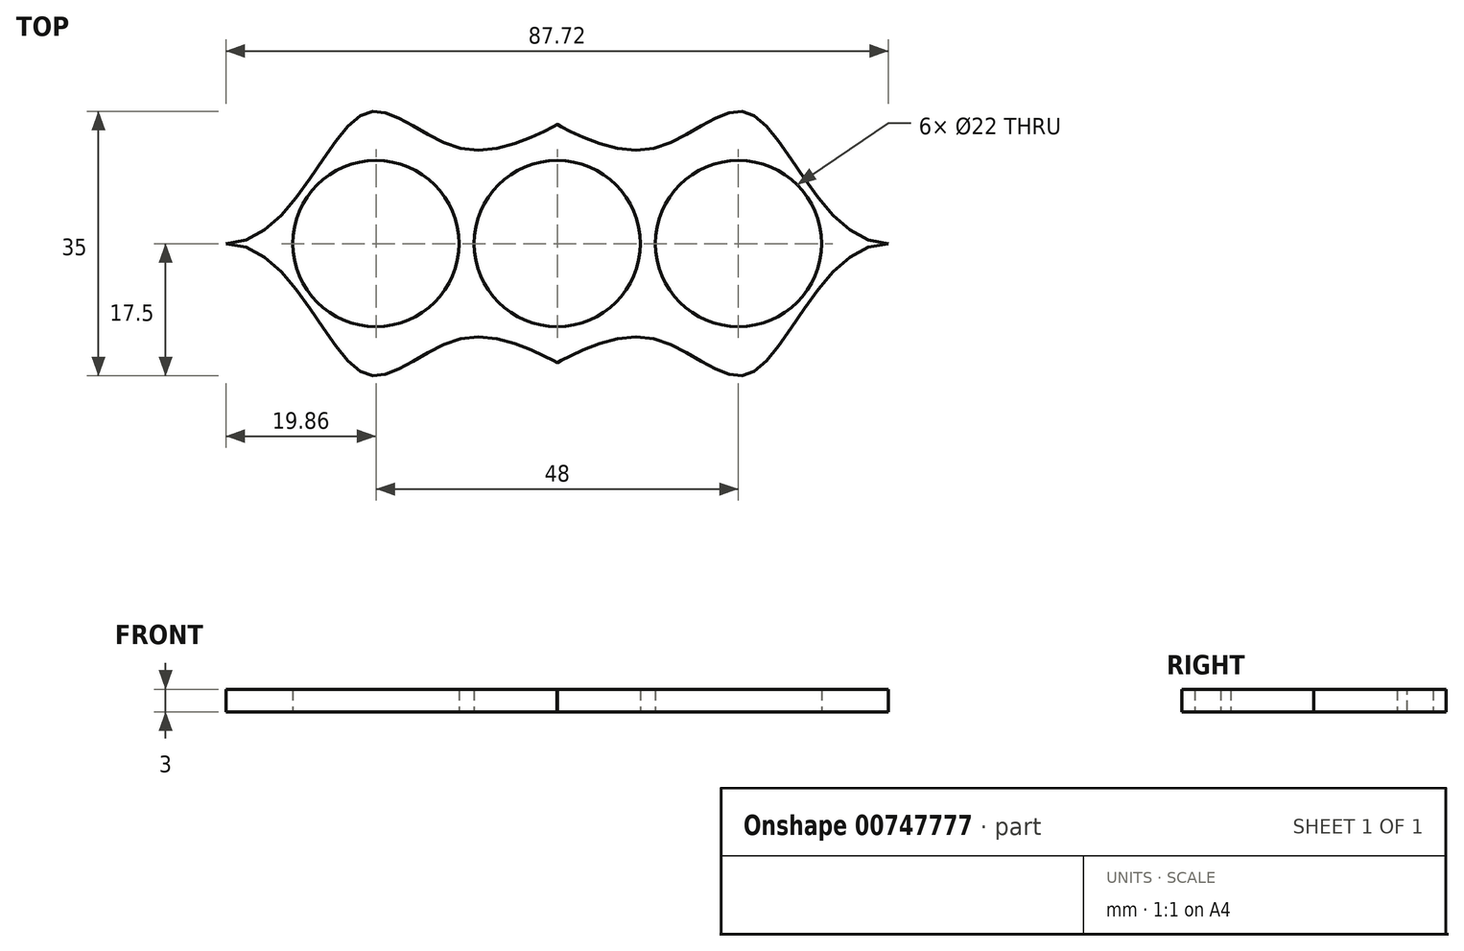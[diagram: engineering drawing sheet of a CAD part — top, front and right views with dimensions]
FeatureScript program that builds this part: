
annotation { "Feature Type Name" : "Feature", "Feature Type Description" : "" }
export const myFeature = defineFeature(function(context is Context, id is Id, definition is map)
    precondition{}
    {
        {
            var Q0;
            Q0=qCreatedBy(makeId("Top.planeOp"),FACE);
            var sketch = newSketch(context, id + "F0", { "sketchPlane" : qUnion([Q0])});
            skCircle(sketch, "E0", {"center": v(0, 0) * mm, "radius": 11 * mm});
            skCircle(sketch, "E1", {"center": v(-24, 0) * mm, "radius": 11 * mm});
            skCircle(sketch, "E2", {"center": v(24, 0) * mm, "radius": 11 * mm});
            skPoint(sketch, "E3.MirrorP", {"position": v(0, -15) * mm});
            skFitSpline(sketch, "E4", {"points": [v(-43.87, 0) * mm, v(-25.51, 17.2) * mm, v(-11.56, 12.4) * mm, v(0, 15.75) * mm, v(0, 15.77) * mm], "startDerivative": vector(66.08, 0) * mm, "endDerivative": vector(-2.95, 5.19) * mm});
            skFitSpline(sketch, "E5.MirrorCS", {"points": [v(-43.87, 0) * mm, v(-25.51, -17.2) * mm, v(-11.56, -12.4) * mm, v(0, -15.75) * mm, v(0, -15.77) * mm], "startDerivative": vector(66.08, 0) * mm, "endDerivative": vector(-2.95, -5.19) * mm});
            skFitSpline(sketch, "E6.MirrorCS", {"points": [v(43.87, 0) * mm, v(25.51, 17.2) * mm, v(11.56, 12.4) * mm, v(0, 15.75) * mm, v(0, 15.77) * mm], "startDerivative": vector(-66.08, 0) * mm, "endDerivative": vector(2.95, 5.19) * mm});
            skFitSpline(sketch, "E7.MirrorCS", {"points": [v(43.87, 0) * mm, v(25.51, -17.2) * mm, v(11.56, -12.4) * mm, v(0, -15.75) * mm, v(0, -15.77) * mm], "startDerivative": vector(-66.08, 0) * mm, "endDerivative": vector(2.95, -5.19) * mm});
            skSolve(sketch);
        }
        {
            var Q0;
            Q0 = qSketchRegion(id + "F0", true);
            extrude(context, id + "F1", {"entities" : qUnion([Q0]), "depth" : 3 * mm, "offsetDistance" : 25 * mm});
        }
        {
            var Q0;
            Q0 = qSketchRegion(id + "F0", true);
            extrude(context, id + "F2", {"entities" : qUnion([Q0]), "depth" : 3 * mm, "offsetDistance" : 25 * mm});
        }
    });
